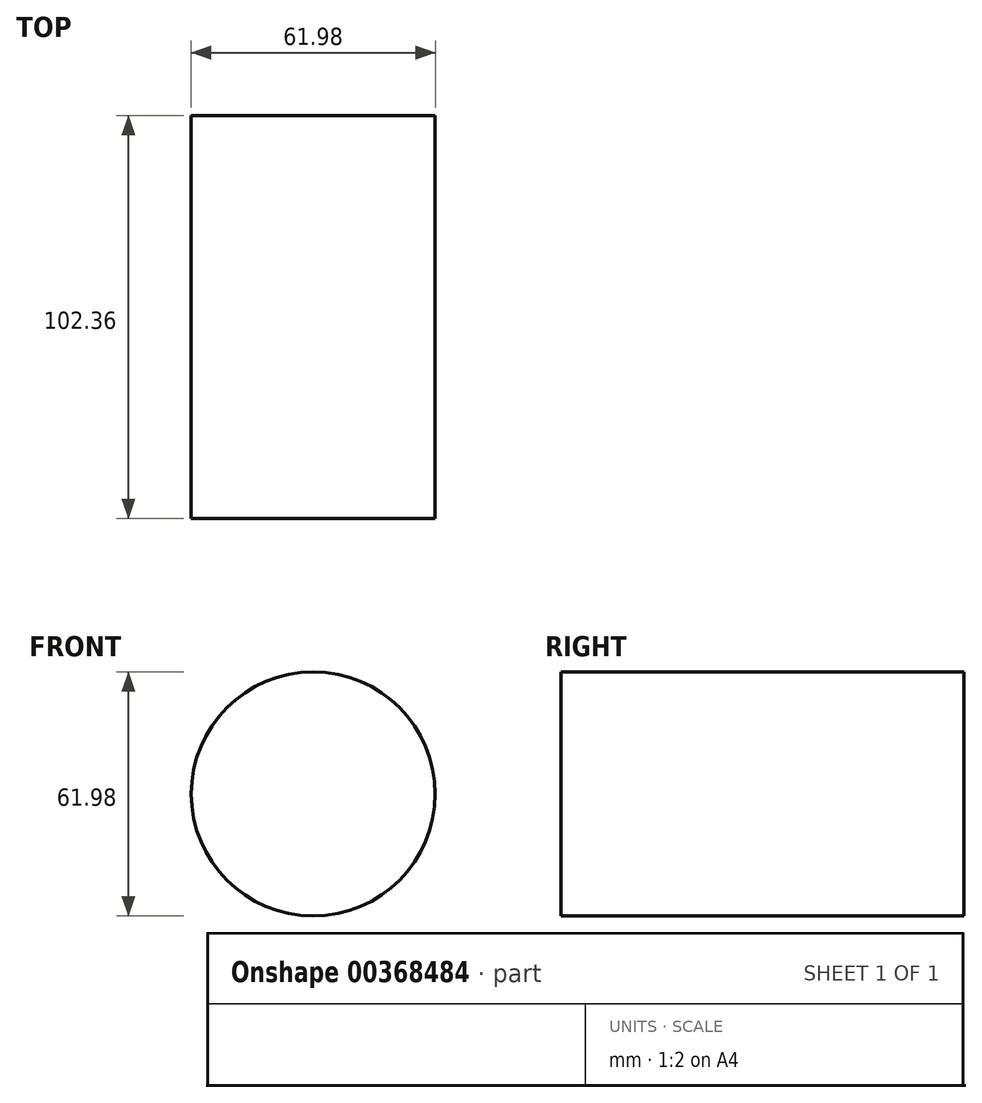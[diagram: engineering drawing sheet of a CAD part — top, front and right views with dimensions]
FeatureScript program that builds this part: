
annotation { "Feature Type Name" : "Feature", "Feature Type Description" : "" }
export const myFeature = defineFeature(function(context is Context, id is Id, definition is map)
    precondition{}
    {
        {
            var Q0;
            Q0=qCreatedBy(makeId("Front.planeOp"),FACE);
            var sketch = newSketch(context, id + "F0", { "sketchPlane" : qUnion([Q0])});
            skCircle(sketch, "E0", {"center": v(-87.14, 17.35) * mm, "radius": 30.99 * mm});
            skSolve(sketch);
        }
        {
            var Q0;
            Q0=makeQuery(id+"F0.imprint","IMPRINT",FACE,{"disambiguationData":[TD([[makeQuery(id+"F0.imprint","IMPRINT",EDGE,{"derivedFrom":sQuery(id+"F0.wireOp",EDGE,"E0")}),1.0]])]});
            extrude(context, id + "F1", {"entities" : qUnion([Q0]), "depth" : 102.36 * mm});
        }
    });
